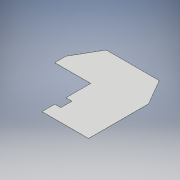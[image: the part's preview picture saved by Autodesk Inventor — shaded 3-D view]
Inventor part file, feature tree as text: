
AUTODESK INVENTOR PART (.ipt)
format: ipt  version: 2018 (Build 220112000, 112)  size: 109,568 bytes
history: native  units: mm
features: extrude x1, sketch x1
ambient origin geometry x8: Origin, YZ Plane, XZ Plane, XY Plane, X Axis, Y Axis, Z Axis, Center Point
bodies: Solid1 (feature_tree)
feature tree (2):
  extrude  "Extrusion1"  Depth=1.6mm
  sketch  "Sketch1"  dims[d0=385.0mm d1=700.0mm d2=346.0mm d3=120.0deg d4=620.0mm d5=346.0mm d6=120.0deg d7=160.0mm d8=150.0mm d9=70.0mm d10=130.0mm d11=70.0mm d12=290.0mm d13=1.6mm d14=0.0mm]
